# Revit family: 1660.741 current
name_source: partatom
category: Plumbing Fixtures
revit_build: Autodesk Revit 2018 (Build: 20170223_1515(x64)
units: mm (PartAtom-declared; Revit-internal decimal feet)

## family parameters
Always vertical = No
Cut with Voids When Loaded = No
OmniClass Number = 23.45.05.14.17
OmniClass Title = Showers
Part Type = Normal
Room Calculation Point = No
Round Connector Dimension = Use Diameter
Shared = Yes
Work Plane-Based = Yes

## types (2) — shared parameters
Assembly Code = D2010700
CW Connection = Yes
CWFU = 3
Default Elevation = 0"
Description = Saving water never goes out of style. This FloWise® single-function handshower complements bathrooms with casual décor. It features our exclusive turbine technology that delivers an invigorating shower using 40% less water, which can save a family up to 8,000 gallons of water a year.
Less Water, More Performance, How refreshing
FloWise® Hand Showers use our exclusive turbine technology to deliver an invigorating shower experience while saving water. These innovative heads can save a family up to 8,000 gallons of water a year.
Flow Rate = 1.5gpm/5.7L/min
HW Connection = Yes
HWFU = 3
IAPMO Compliance = ASME A112.18.1, CSA 125.1, cUPC
Length = 9 3/8"
Manufacturer = American Standard
NPSM Connection Size = 1/2"
Price = Prices may vary. Please consult Manufacturer Representative for most up-to-date price list.
Product Documentation Link = https://www.americanstandard-us.com
Product Page URL = https://www.americanstandard-us.com
URL = https://www.americanstandard-us.com
Vent Connection = No
WFU = 4
Warranty Information URL = https://www.americanstandard-us.com
Waste Connection = No
Width = 2 1/2"

## per-type parameters (varying)
| type | Finish | Material |
| 1660.741.002 | Metal-American Standard-Brass-002-Polished Chrome | Metal-American Standard-Brass-002-Polished Chrome |
| 1660.741.295 | Metal-American Standard-Brass-295-Brushed Nickel | Metal-American Standard-Brass-295-Brushed Nickel |

note: column(s) folded — value = type name in every type: Model

## geometry (parser evidence)
native form markers: Sweep x2
no freeform markers — native parametric forms only
